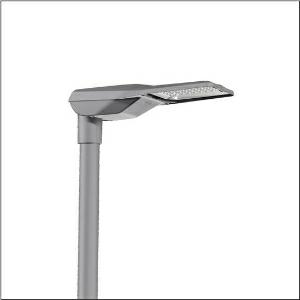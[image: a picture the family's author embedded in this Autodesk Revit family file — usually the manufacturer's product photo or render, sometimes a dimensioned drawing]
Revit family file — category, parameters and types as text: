
# Revit family: streetlight_sl_21_iq_mini___st1_5a_5xe2p41d08gb_b9bd
name_source: partatom
category: Lighting Fixtures
units: mm (PartAtom-declared; Revit-internal decimal feet)

## family parameters
Cut with Voids When Loaded = No
Host = Face
Light Source = No
Part Type = Normal
Room Calculation Point = No
Round Connector Dimension = Use Diameter
Shared = No

## types (1)
- --- (1 x LED, 5810 lm, 37.1 W, 4000K)
    Apparent Load = 37 VA
    CIE Flux Codes = 22 53 95 100 100
    Color Rendering = 70
    Color Temperature = 4000K
    Default Elevation = 1800 mm
    Description = Streetlight SL 21 iQ mini, mast luminaire, primary light control with lens, of PMMA, primary optical cover: cover, of toughened safety glass, transparent, light distribution: ST1.5a, light emission: direct distribution, primary light characteristic: asymmetric, installation type: post-top, side-entry, LED, High Power LED, rated luminous flux: 5.810lm, luminous efficacy: 157lm/W, light colour: 740, colour temperature: 4000K, control gear: iQ-Comfort, control: Auto-Match, Temp-Guard, Lumen-Switch, Night-Set, Smart-Wire, Light-Fading, Desk-Remote (wireless, voltage-free reading and setting of iQ features in the workshop via application-optimized NFC function/RFID function), optimised constant luminous flux control (CLO 2.0), pre-setting: linear dimming characteristic, mains connection: 220..240V, AC, 50/60Hz, start of lifetime: 37W, end of service life: 39W, reduction: 18W, luminaire housing, of diecast aluminium, powder-coated, Siteco® metallic grey (DB 702S), corrosivity category C5 mid according to DIN EN ISO 12944, please order mast flange separately, inclination adjustable: 0°, 5°, 10°, 15°, sealing non-destructively replaceable, multi-level sealing system, length: 628mm, width: 235mm, height: 110mm, mast flange for spigot size: 42mm (side-entry): 5XC10008XM4, 60/48mm (side-entry/post-top): 5XC10108XM2, 76/60mm (side-entry/post-top): 5XC10108XM1, mounting height: 4..8m, protection rating (complete): IP66, insulation class (complete): insulation class II (safety insulation), certification: CE, ENEC, ENEC+, VDE, impact resistance: IK10, permissible operating ambient temperature for outdoor applications: -40..+50°C, standard-compliant lighting for roads and squares, packaging unit: 1 piece

Light Distribution: ST1.5a
    Height = 110 mm
    Lamp = 1 x LED
    Lamp Light Flux = 5810 lm
    Lamp Power = 37.1 W
    Lamp count = 1
    Length = 625 mm
    Luminous efficacy = 157 lm/W
    Manufacturer = Siteco
    ModVariant = No
    Model = 5XE2P41D08GB
    Number of Poles = 1
    OnlyDefault = Yes
    Power Factor = 1
    Product Name = Streetlight SL 21 iQ mini | ST1.5a
    Product group = mast luminaire | pylon top
    ProductGroupID = 6100
    Protection Class = Protection class II
    Protection Degree = IP 66
    RLX_Detail_Level = 1
    RLX_Emergency_Light_Flux = 0 lm
    RLX_Emergency_Type = 0
    RLX_Emergency_Type_DB = No
    RlxData = <blob elided: 29865 chars, md5=0a0d118f>
    Socket = socket
    Standby Power = 0 W
    System Light Flux = 5810 lm
    System Power = 37 W
    Type Comments = factory setting: luminous flux: 100 % | dim-lin: 254 | 385 mA
    Type Image = l_1003519.jpg
    URL = http://relux.com
    VarID = @adj_197263
    Voltage = 0 V
    Weight = 0.00 kg
    Width = 234 mm

## geometry (parser evidence)
native form markers: Blend x4, Sweep x10
no freeform markers — native parametric forms only
